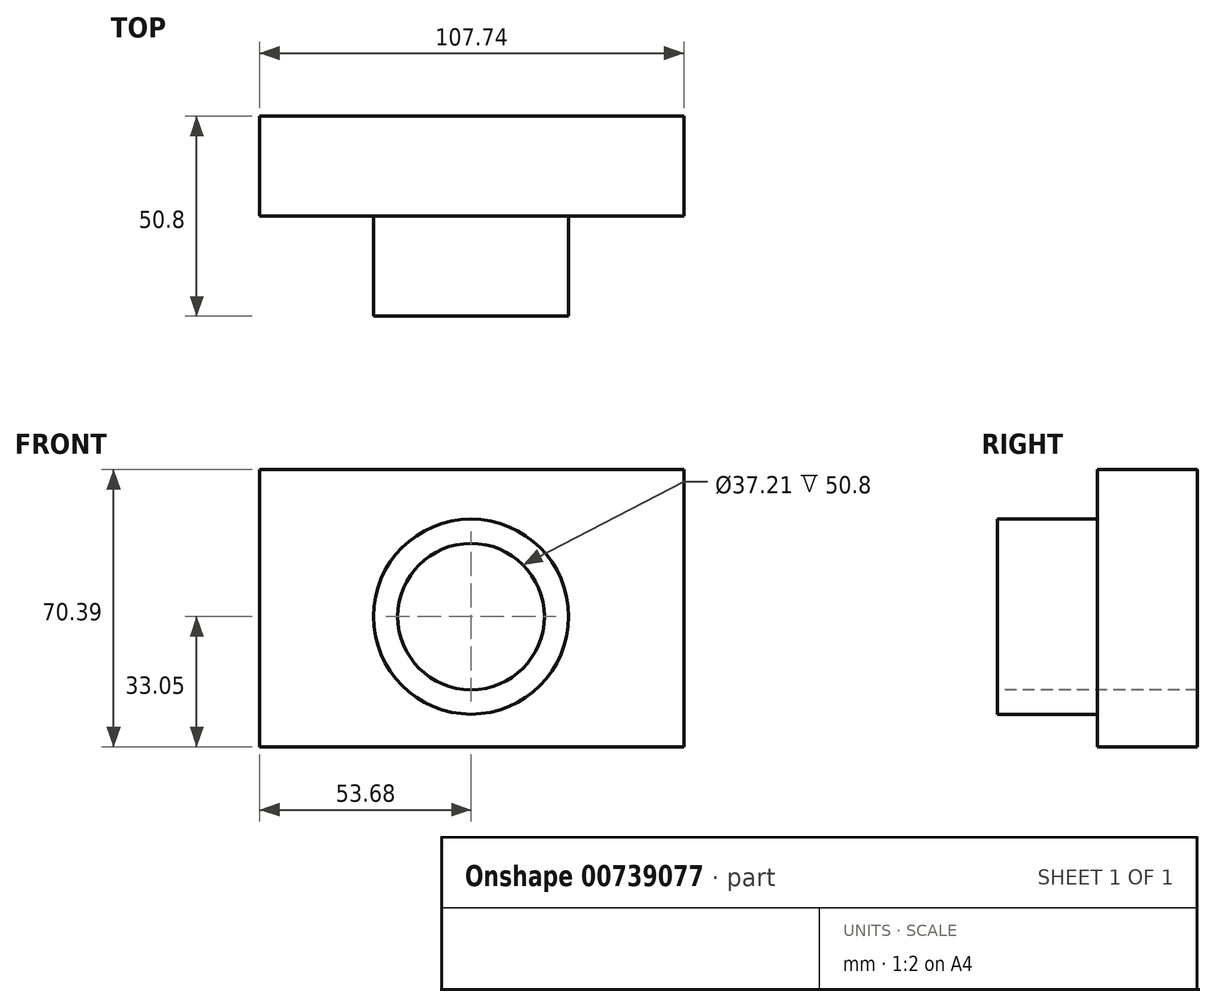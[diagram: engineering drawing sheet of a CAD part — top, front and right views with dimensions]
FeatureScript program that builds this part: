
annotation { "Feature Type Name" : "Feature", "Feature Type Description" : "" }
export const myFeature = defineFeature(function(context is Context, id is Id, definition is map)
    precondition{}
    {
        {
            var Q0;
            Q0=qCreatedBy(makeId("Front.planeOp"),FACE);
            var sketch = newSketch(context, id + "F0", { "sketchPlane" : qUnion([Q0])});
            skLineSegment(sketch, "E0.bottom", {"start": v(-53.68, 37.34) * mm, "end": v(54.06, 37.34) * mm});
            skLineSegment(sketch, "E0.top", {"start": v(-53.68, -33.05) * mm, "end": v(54.06, -33.05) * mm});
            skLineSegment(sketch, "E0.left", {"start": v(-53.68, 37.34) * mm, "end": v(-53.68, -33.05) * mm});
            skLineSegment(sketch, "E0.right", {"start": v(54.06, 37.34) * mm, "end": v(54.06, -33.05) * mm});
            skSolve(sketch);
        }
        {
            var Q0;
            Q0=makeQuery(id+"F0.imprint","IMPRINT",FACE,{"disambiguationData":[TD([[makeQuery(id+"F0.imprint","IMPRINT",EDGE,{"derivedFrom":sQuery(id+"F0.wireOp",EDGE,"E0.bottom")}),-1.0]])]});
            extrude(context, id + "F1", {"entities" : qUnion([Q0]), "depth" : 25.4 * mm, "offsetDistance" : 25.4 * mm});
        }
        {
            var Q0;
            Q0=makeQuery(id+"F1.opExtrude","CAP_FACE",FACE,{"disambiguationData":[OSD([sQuery(id+"F0.wireOp",EDGE,"E0.bottom"),sQuery(id+"F0.wireOp",EDGE,"E0.top"),sQuery(id+"F0.wireOp",EDGE,"E0.left"),sQuery(id+"F0.wireOp",EDGE,"E0.right")])],"isStart":false});
            var sketch = newSketch(context, id + "F2", { "sketchPlane" : qUnion([Q0])});
            skCircle(sketch, "E1", {"center": v(0, 0) * mm, "radius": 24.78 * mm});
            skSolve(sketch);
        }
        {
            var Q0;
            Q0 = qSketchRegion(id + "F2", true);
            var Q1;
            Q1=makeQuery(id+"F2.imprint","IMPRINT",FACE,{"disambiguationData":[TD([[makeQuery(id+"F2.imprint","IMPRINT",EDGE,{"derivedFrom":sQuery(id+"F2.wireOp",EDGE,"E1")}),1.0]])]});
            extrude(context, id + "F3", {"entities" : qUnion([Q0, Q1]), "operationType" : NewBodyOperationType.ADD, "depth" : 25.4 * mm, "offsetDistance" : 25.4 * mm});
        }
        {
            var Q0;
            Q0=makeQuery(id+"F3.opExtrude","CAP_FACE",FACE,{"disambiguationData":[OSD([sQuery(id+"F2.wireOp",EDGE,"E1")])],"isStart":false});
            var sketch = newSketch(context, id + "F4", { "sketchPlane" : qUnion([Q0])});
            skCircle(sketch, "E2", {"center": v(0, 0) * mm, "radius": 18.6 * mm});
            skSolve(sketch);
        }
        {
            var Q0;
            Q0 = qSketchRegion(id + "F4", true);
            extrude(context, id + "F5", {"entities" : qUnion([Q0]), "operationType" : NewBodyOperationType.REMOVE, "oppositeDirection" : true, "depth" : 76.2 * mm, "offsetDistance" : 25.4 * mm});
        }
    });
